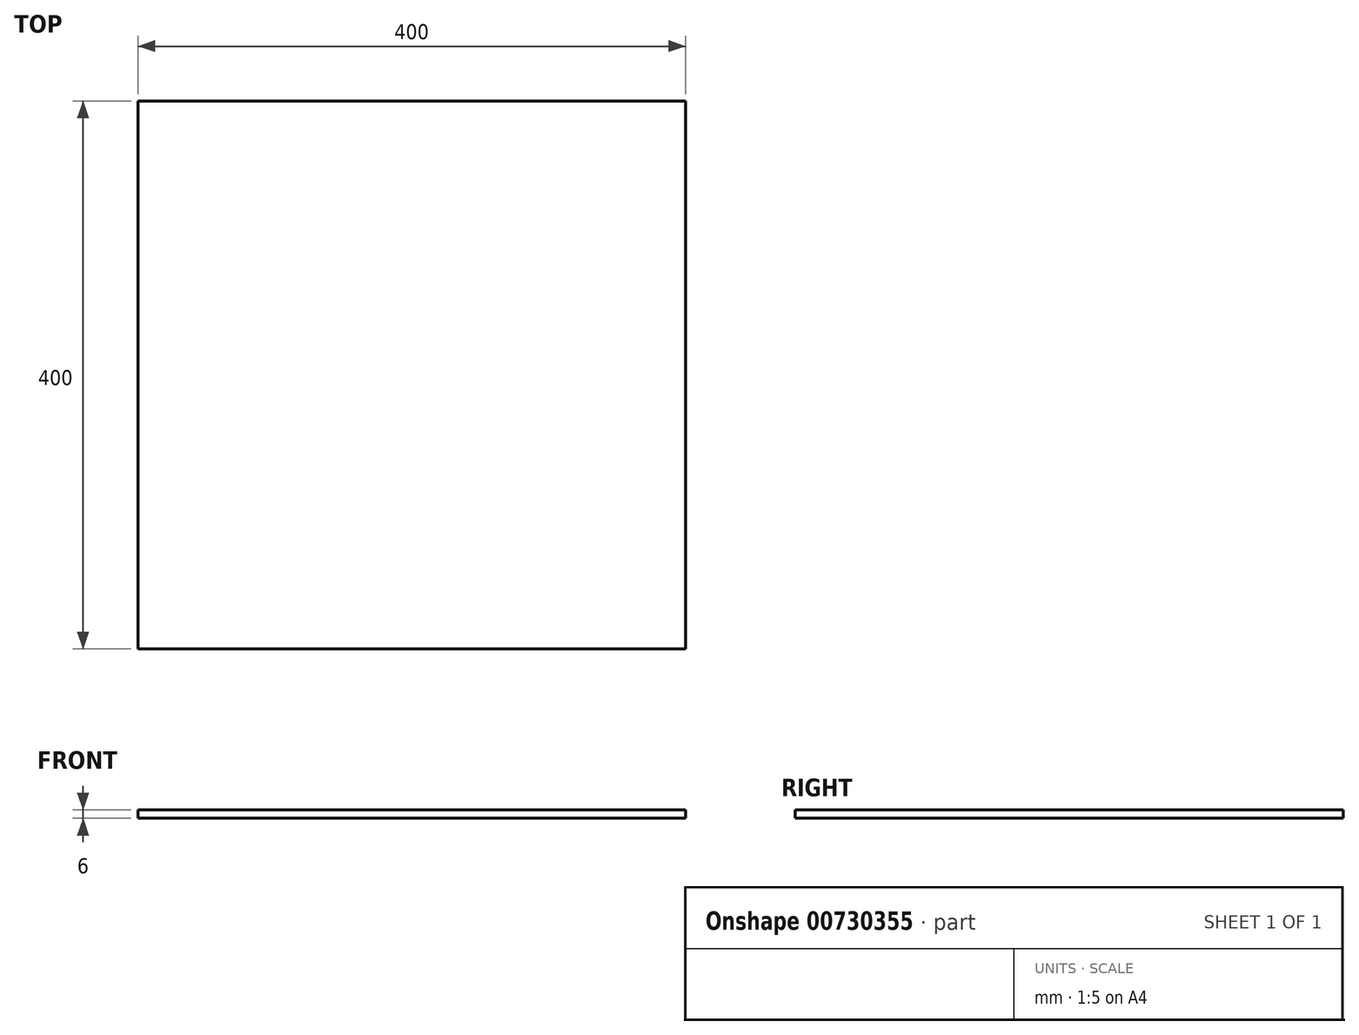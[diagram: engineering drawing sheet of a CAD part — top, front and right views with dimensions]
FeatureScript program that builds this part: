
annotation { "Feature Type Name" : "Feature", "Feature Type Description" : "" }
export const myFeature = defineFeature(function(context is Context, id is Id, definition is map)
    precondition{}
    {
        {
            var Q0;
            Q0=qCreatedBy(makeId("Top.planeOp"),FACE);
            var sketch = newSketch(context, id + "F0", { "sketchPlane" : qUnion([Q0])});
            skLineSegment(sketch, "E0.bottom", {"start": v(-200, 200) * mm, "end": v(200, 200) * mm});
            skLineSegment(sketch, "E0.top", {"start": v(-200, -200) * mm, "end": v(200, -200) * mm});
            skLineSegment(sketch, "E0.left", {"start": v(-200, 200) * mm, "end": v(-200, -200) * mm});
            skLineSegment(sketch, "E0.right", {"start": v(200, 200) * mm, "end": v(200, -200) * mm});
            skSolve(sketch);
        }
        {
            var Q0;
            Q0=makeQuery(id+"F0.imprint","IMPRINT",FACE,{"disambiguationData":[TD([[makeQuery(id+"F0.imprint","IMPRINT",EDGE,{"derivedFrom":sQuery(id+"F0.wireOp",EDGE,"E0.bottom")}),-1.0]])]});
            extrude(context, id + "F1", {"entities" : qUnion([Q0]), "depth" : 6 * mm, "offsetDistance" : 25 * mm});
        }
    });
